# Revit family: Geryon SRD-C01
name_source: partatom
category: Türen
revit_build: Autodesk Revit 2016 (Build: 20150220_1215(x64)
units: mm (PartAtom-declared; Revit-internal decimal feet)

## family parameters
Beim Laden mit Abzugskörper schneiden = Nein
Gemeinsam genutzt = Nein
Immer vertikal = Ja
OmniClass-Nummer = 23.30.10.00
OmniClass-Titel = Doors
Raumberechnungspunkt = Nein

## types (6) — shared parameters
Analytische Konstruktion = <Keine Auswahl>
CoverMaterial = Glas
Date of publishing = 1/16/2017
Design country = Germany
Dicke = 63 mm  [stored 0.206693 ft]
Edition number = 1
ElementWeight = 0.00 kg
FrameMaterial = 1.4401 - A4
Funktion = Außen
HasLock 120 = Nein
HasLockInside = Nein
HasLockInside 120 = Nein
HasLockInside 180 = Nein
HasShellTopFrame = Ja
HasShutOffDevice = Nein
HasShutOffDeviceInside = Nein
HasShutOffDeviceInside120 = Nein
HasShutOffDeviceInside180 = Nein
Hersteller = Kaba GmbH
Konstruktionstyp = Revolving Door
Manufacturer = Kaba GmbH
Manufacturer country = Germany
Manufacturer name = DORMA
Material main = Metal
Material secondary = Glass
Modell = Talos RDR-E01
Nominal height = 2300
OperatingWeight = 0.00 kg
Product SKU = Geryon_SRD-C01
RubberMaterial = Zellkautschuk - EPDM
SectionWidth = 4300 mm
Technical description = http://www.kaba.com
Type = Geryon SRD-E01
URL = http://www.kaba.com
Weight = 0.00 kg
zero-valued in all types: Nominal width

## per-type parameters (varying)
- SRD-C01 1520: AccessLengthOrRadius=710 mm; BaseType=139; ClearHeight=2700 mm; ConsoleS1=751 mm; ConsoleS2=751 mm; ConsoleType=console : Type 5; CoverWidth=200 mm  [stored 0.656168 ft]; Diameter=730 mm; DiameterCoverFront=810 mm; DiameterGlassInside=719 mm; DiameterGlassOutside=730 mm; DiameterNightLock=760 mm; DiameterNightLockCover=790 mm  [stored 2.59186 ft]; DiameterNightLockFrame=751 mm; DiameterNightLockGlassInside=769 mm  [stored 2.52297 ft]; DiameterNightLockGlassOutside=780 mm; DiameterOutside=740 mm; DoorThickness=40 mm  [stored 0.131234 ft]; DoorWidth=670 mm; FrameThickness=63 mm  [stored 0.206693 ft]; FrameThicknessCenter=75 mm; GasShellTopFrame 120=Nein; HandleMaterial=1.4401 - A4; HasCentralColumn=Ja; HasCentralColumn 120=Nein; HasCentralColumn 180=Ja; HasConsoleS1=Ja; HasConsoleS1 120=Nein; HasConsoleS1 180=Ja; HasConsoleS2=Ja; HasConsoleS2 120=Nein; HasConsoleS2 180=Ja; HasGrabHandles=Nein; HasGrabHandles 120=Nein; HasGrabHandles 180=Ja; HasHandleBar=Ja; HasLock=Nein; HasLock 180=Nein; HasShellTopFrame 180=Ja; Height=2900 mm; MotorDriveType=K8-SA2; OuterDiameter=2000 mm; ProfileCenter=0 mm  [stored 0 ft]; ProfileWidth=40 mm  [stored 0.131234 ft]; RotationInterval 120=Nein; RotationInterval 180=Ja; StandardUsed=3; Width=1520 mm
- SRD-C01 1620: AccessLengthOrRadius=760 mm; BaseType=109 mm; ClearHeight=2600 mm; ConsoleS1=801 mm; ConsoleS2=801 mm; ConsoleType=console : Type 4; CoverWidth=300 mm; Diameter=780 mm; DiameterCoverFront=860 mm; DiameterGlassInside=769 mm  [stored 2.52297 ft]; DiameterGlassOutside=780 mm; DiameterNightLock=810 mm; DiameterNightLockCover=840 mm  [stored 2.75591 ft]; DiameterNightLockFrame=801 mm; DiameterNightLockGlassInside=819 mm  [stored 2.68701 ft]; DiameterNightLockGlassOutside=830 mm; DiameterOutside=790 mm  [stored 2.59186 ft]; DoorThickness=25 mm  [stored 0.082021 ft]; DoorWidth=720 mm; FrameThickness=35 mm  [stored 0.114829 ft]; FrameThicknessCenter=47 mm; GasShellTopFrame 120=Ja; HandleMaterial=1.4401 - A4; HasCentralColumn=Nein; HasCentralColumn 120=Nein; HasCentralColumn 180=Nein; HasConsoleS1=Ja; HasConsoleS1 120=Ja; HasConsoleS1 180=Nein; HasConsoleS2=Ja; HasConsoleS2 120=Ja; HasConsoleS2 180=Nein; HasGrabHandles=Ja; HasGrabHandles 120=Ja; HasGrabHandles 180=Nein; HasHandleBar=Nein; HasLock=Nein; HasLock 180=Nein; HasShellTopFrame 180=Nein; Height=2900 mm; MotorDriveType=K8-SA1; OuterDiameter=1800 mm; ProfileCenter=7.5 mm; ProfileWidth=40 mm  [stored 0.131234 ft]; RotationInterval 120=Ja; RotationInterval 180=Nein; StandardUsed=2; Width=1620 mm
- SRD-C01 2020: AccessLengthOrRadius=960 mm; BaseType=150; ClearHeight=2100 mm; ConsoleS1=1001 mm; ConsoleS2=1001 mm; ConsoleType=console : Type 4; CoverWidth=200 mm  [stored 0.656168 ft]; Diameter=980 mm; DiameterCoverFront=1060 mm; DiameterGlassInside=969 mm; DiameterGlassOutside=980 mm; DiameterNightLock=1010 mm; DiameterNightLockCover=1040 mm; DiameterNightLockFrame=1001 mm; DiameterNightLockGlassInside=1019 mm; DiameterNightLockGlassOutside=1030 mm; DiameterOutside=990 mm; DoorThickness=56 mm  [stored 0.183727 ft]; DoorWidth=920 mm; FrameThickness=80 mm  [stored 0.262467 ft]; FrameThicknessCenter=92 mm  [stored 0.301837 ft]; GasShellTopFrame 120=Nein; HandleMaterial=1.4401 - A4; HasCentralColumn=Nein; HasCentralColumn 120=Nein; HasCentralColumn 180=Nein; HasConsoleS1=Nein; HasConsoleS1 120=Nein; HasConsoleS1 180=Nein; HasConsoleS2=Nein; HasConsoleS2 120=Nein; HasConsoleS2 180=Nein; HasGrabHandles=Nein; HasGrabHandles 120=Nein; HasGrabHandles 180=Ja; HasHandleBar=Ja; HasLock=Nein; HasLock 180=Nein; HasShellTopFrame 180=Ja; Height=2300 mm; OuterDiameter=3000 mm; ProfileCenter=0 mm  [stored 0 ft]; ProfileWidth=56 mm  [stored 0.183727 ft]; RotationInterval 120=Nein; RotationInterval 180=Ja; StandardUsed=8; Width=2020 mm
- SRD-C01 1720: AccessLengthOrRadius=810 mm; BaseType=220; ClearHeight=2400 mm; ConsoleS1=851 mm; ConsoleS2=851 mm; ConsoleType=console : Type 5; CoverWidth=300 mm; Diameter=830 mm; DiameterCoverFront=910 mm; DiameterGlassInside=819 mm  [stored 2.68701 ft]; DiameterGlassOutside=830 mm; DiameterNightLock=860 mm; DiameterNightLockCover=890 mm  [stored 2.91995 ft]; DiameterNightLockFrame=851 mm; DiameterNightLockGlassInside=869 mm; DiameterNightLockGlassOutside=880 mm; DiameterOutside=840 mm  [stored 2.75591 ft]; DoorThickness=25 mm  [stored 0.082021 ft]; DoorWidth=770 mm; FrameThickness=49 mm  [stored 0.160761 ft]; FrameThicknessCenter=61 mm; GasShellTopFrame 120=Nein; HandleMaterial=1.4401 - A4; HasCentralColumn=Ja; HasCentralColumn 120=Nein; HasCentralColumn 180=Ja; HasConsoleS1=Nein; HasConsoleS1 120=Nein; HasConsoleS1 180=Nein; HasConsoleS2=Nein; HasConsoleS2 120=Nein; HasConsoleS2 180=Nein; HasGrabHandles=Nein; HasGrabHandles 120=Nein; HasGrabHandles 180=Ja; HasHandleBar=Ja; HasLock=Nein; HasLock 180=Nein; HasShellTopFrame 180=Ja; Height=2700 mm; MotorDriveType=K8-SA1; OuterDiameter=2200 mm; ProfileCenter=7.5 mm; ProfileWidth=40 mm  [stored 0.131234 ft]; RotationInterval 120=Nein; RotationInterval 180=Ja; StandardUsed=4; Width=1720 mm
- SRD-C01 1820: AccessLengthOrRadius=860 mm; BaseType=220; ClearHeight=2100 mm; ConsoleS1=901 mm; ConsoleS2=949 mm; ConsoleType=console : Type 5; CoverWidth=200 mm  [stored 0.656168 ft]; Diameter=880 mm; DiameterCoverFront=960 mm; DiameterGlassInside=869 mm; DiameterGlassOutside=880 mm; DiameterNightLock=910 mm; DiameterNightLockCover=940 mm; DiameterNightLockFrame=901 mm; DiameterNightLockGlassInside=919 mm; DiameterNightLockGlassOutside=930 mm; DiameterOutside=890 mm  [stored 2.91995 ft]; DoorThickness=40 mm  [stored 0.131234 ft]; DoorWidth=820 mm; FrameThickness=63 mm  [stored 0.206693 ft]; FrameThicknessCenter=75 mm; GasShellTopFrame 120=Nein; HandleMaterial=PA6.6 Gf30(schwarz); HasCentralColumn=Ja; HasCentralColumn 120=Nein; HasCentralColumn 180=Ja; HasConsoleS1=Nein; HasConsoleS1 120=Nein; HasConsoleS1 180=Nein; HasConsoleS2=Nein; HasConsoleS2 120=Nein; HasConsoleS2 180=Nein; HasGrabHandles=Ja; HasGrabHandles 120=Nein; HasGrabHandles 180=Ja; HasHandleBar=Nein; HasLock=Ja; HasLock 180=Ja; HasShellTopFrame 180=Ja; Height=2300 mm; MotorDriveType=K8-SA1; OuterDiameter=2400 mm; ProfileCenter=0 mm  [stored 0 ft]; ProfileWidth=40 mm  [stored 0.131234 ft]; RotationInterval 120=Nein; RotationInterval 180=Ja; StandardUsed=5; Width=1820 mm
- SRD-C01 1920: AccessLengthOrRadius=910 mm; BaseType=250; ClearHeight=2800 mm; ConsoleS1=951 mm; ConsoleS2=951 mm; ConsoleType=console : Type 4; CoverWidth=300 mm; Diameter=930 mm; DiameterCoverFront=1010 mm; DiameterGlassInside=919 mm; DiameterGlassOutside=930 mm; DiameterNightLock=960 mm; DiameterNightLockCover=990 mm; DiameterNightLockFrame=951 mm; DiameterNightLockGlassInside=969 mm; DiameterNightLockGlassOutside=980 mm; DiameterOutside=940 mm; DoorThickness=56 mm  [stored 0.183727 ft]; DoorWidth=870 mm  [stored 2.85433 ft]; FrameThickness=80 mm  [stored 0.262467 ft]; FrameThicknessCenter=92 mm  [stored 0.301837 ft]; GasShellTopFrame 120=Ja; HandleMaterial=1.4401 - A4; HasCentralColumn=Ja; HasCentralColumn 120=Ja; HasCentralColumn 180=Nein; HasConsoleS1=Ja; HasConsoleS1 120=Ja; HasConsoleS1 180=Nein; HasConsoleS2=Ja; HasConsoleS2 120=Ja; HasConsoleS2 180=Nein; HasGrabHandles=Nein; HasGrabHandles 120=Ja; HasGrabHandles 180=Nein; HasHandleBar=Ja; HasLock=Nein; HasLock 180=Nein; HasShellTopFrame 180=Nein; Height=3100 mm; OuterDiameter=2800 mm; ProfileCenter=0 mm  [stored 0 ft]; ProfileWidth=56 mm  [stored 0.183727 ft]; RotationInterval 120=Ja; RotationInterval 180=Nein; StandardUsed=7; Width=1920 mm

note: [stored X ft] marks values corroborated as IEEE doubles in the binary element streams (Revit-internal decimal feet)
